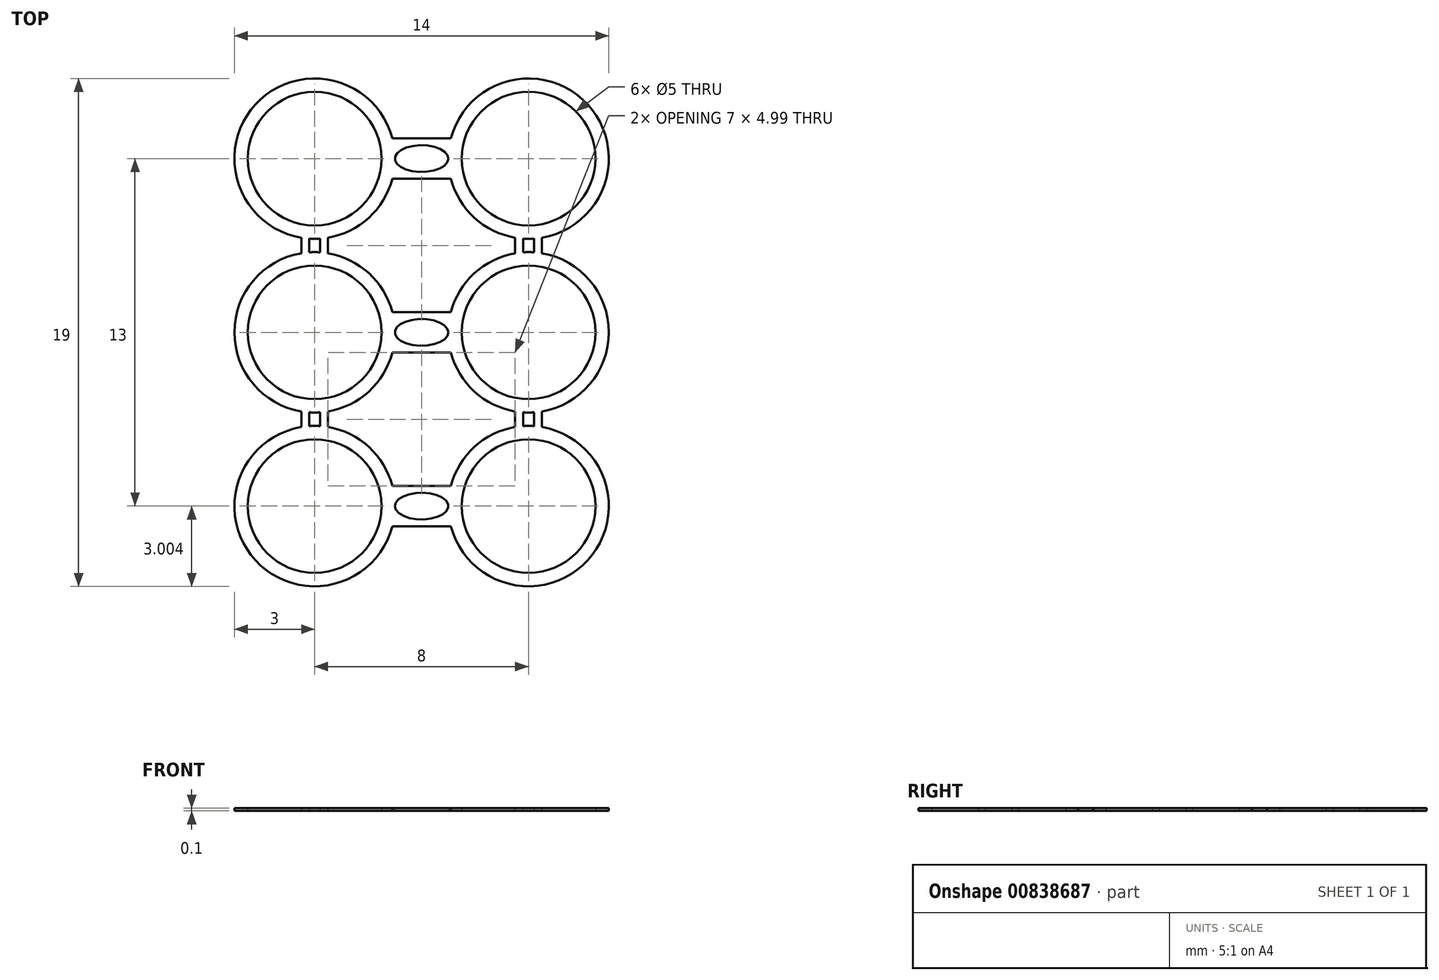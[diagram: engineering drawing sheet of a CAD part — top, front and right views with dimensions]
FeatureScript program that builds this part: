
annotation { "Feature Type Name" : "Feature", "Feature Type Description" : "" }
export const myFeature = defineFeature(function(context is Context, id is Id, definition is map)
    precondition{}
    {
        {
            var Q0;
            Q0=qCreatedBy(makeId("Top.planeOp"),FACE);
            var sketch = newSketch(context, id + "F0", { "sketchPlane" : qUnion([Q0])});
            skCircle(sketch, "E0", {"center": v(-50.37, 50.6) * mm, "radius": 3 * mm});
            skCircle(sketch, "E1", {"center": v(-50.37, 57.1) * mm, "radius": 3 * mm});
            skCircle(sketch, "E2", {"center": v(-50.37, 44.1) * mm, "radius": 3 * mm});
            skCircle(sketch, "E3", {"center": v(-42.37, 50.6) * mm, "radius": 3 * mm});
            skCircle(sketch, "E4", {"center": v(-42.37, 44.1) * mm, "radius": 3 * mm});
            skCircle(sketch, "E5", {"center": v(-42.37, 50.6) * mm, "radius": 2.5 * mm});
            skCircle(sketch, "E6", {"center": v(-50.37, 50.6) * mm, "radius": 2.5 * mm});
            skCircle(sketch, "E7", {"center": v(-50.37, 44.1) * mm, "radius": 2.5 * mm});
            skCircle(sketch, "E8", {"center": v(-42.37, 44.1) * mm, "radius": 2.5 * mm});
            skCircle(sketch, "E9", {"center": v(-50.37, 57.1) * mm, "radius": 2.5 * mm});
            skCircle(sketch, "E10", {"center": v(-42.37, 57.1) * mm, "radius": 3 * mm});
            skCircle(sketch, "E11", {"center": v(-42.37, 57.1) * mm, "radius": 2.5 * mm});
            skLineSegment(sketch, "E12", {"start": v(-47.47, 43.34) * mm, "end": v(-45.27, 43.34) * mm});
            skLineSegment(sketch, "E13", {"start": v(-47.47, 44.85) * mm, "end": v(-45.27, 44.85) * mm});
            skLineSegment(sketch, "E14", {"start": v(-47.47, 49.84) * mm, "end": v(-45.27, 49.84) * mm});
            skLineSegment(sketch, "E15", {"start": v(-47.47, 51.35) * mm, "end": v(-45.27, 51.35) * mm});
            skLineSegment(sketch, "E16", {"start": v(-47.47, 56.34) * mm, "end": v(-45.27, 56.34) * mm});
            skLineSegment(sketch, "E17", {"start": v(-47.47, 57.85) * mm, "end": v(-45.27, 57.85) * mm});
            skLineSegment(sketch, "E18", {"start": v(-42.37, 38.05) * mm, "end": v(-41.87, 38.05) * mm});
            skLineSegment(sketch, "E19", {"start": v(-49.87, 47.05) * mm, "end": v(-49.87, 47.64) * mm});
            skLineSegment(sketch, "E20", {"start": v(-50.87, 47.05) * mm, "end": v(-50.87, 47.64) * mm});
            skPoint(sketch, "E21.start.orphan", {"position": v(-50.37, 38.05) * mm});
            skLineSegment(sketch, "E22.trimOffspring", {"start": v(-42.87, 47.05) * mm, "end": v(-42.87, 47.64) * mm});
            skLineSegment(sketch, "E23.trimOffspring", {"start": v(-41.87, 47.05) * mm, "end": v(-41.87, 47.64) * mm});
            skLineSegment(sketch, "E24.trimOffspring", {"start": v(-50.87, 53.55) * mm, "end": v(-50.87, 54.14) * mm});
            skLineSegment(sketch, "E25.trimOffspring", {"start": v(-49.87, 53.55) * mm, "end": v(-49.87, 54.14) * mm});
            skLineSegment(sketch, "E26.trimOffspring", {"start": v(-42.87, 53.55) * mm, "end": v(-42.87, 54.14) * mm});
            skLineSegment(sketch, "E27.trimOffspring", {"start": v(-41.87, 53.55) * mm, "end": v(-41.87, 54.14) * mm});
            skLineSegment(sketch, "E28", {"start": v(-50.57, 47.34) * mm, "end": v(-50.57, 47.09) * mm});
            skLineSegment(sketch, "E29", {"start": v(-50.17, 47.34) * mm, "end": v(-50.17, 47.09) * mm});
            skLineSegment(sketch, "E30.trimOffspring", {"start": v(-50.57, 53.59) * mm, "end": v(-50.57, 54.1) * mm});
            skLineSegment(sketch, "E31.trimOffspring", {"start": v(-50.17, 53.59) * mm, "end": v(-50.17, 54.1) * mm});
            skLineSegment(sketch, "E32", {"start": v(-50.17, 47.34) * mm, "end": v(-50.17, 47.6) * mm});
            skLineSegment(sketch, "E33", {"start": v(-50.57, 47.34) * mm, "end": v(-50.57, 47.6) * mm});
            skLineSegment(sketch, "E34", {"start": v(-42.57, 47.09) * mm, "end": v(-42.57, 47.6) * mm});
            skLineSegment(sketch, "E35", {"start": v(-42.17, 47.09) * mm, "end": v(-42.17, 47.6) * mm});
            skLineSegment(sketch, "E36.trimOffspring", {"start": v(-42.57, 53.59) * mm, "end": v(-42.57, 54.1) * mm});
            skLineSegment(sketch, "E37.trimOffspring", {"start": v(-42.17, 53.59) * mm, "end": v(-42.17, 54.1) * mm});
            skEllipse(sketch, "E38", {"center": v(-46.37, 57.1) * mm, "majorRadius": 1 * mm, "minorRadius": 0.5 * mm, "majorAxis": v(-1, 0)});
            skPoint(sketch, "E38.centerSnap0", {"position": v(-47.47, 57.1) * mm});
            skPoint(sketch, "E38.centerSnap1", {"position": v(-46.37, 56.34) * mm});
            skEllipse(sketch, "E39.MirrorC", {"center": v(-46.37, 44.1) * mm, "majorRadius": 1 * mm, "minorRadius": 0.5 * mm, "majorAxis": v(-1, 0)});
            skEllipse(sketch, "E40.MirrorC", {"center": v(-46.37, 50.6) * mm, "majorRadius": 1 * mm, "minorRadius": 0.5 * mm, "majorAxis": v(-1, 0)});
            skSolve(sketch);
        }
        {
            var Q0;
            Q0=makeQuery(id+"F0.imprint","IMPRINT",FACE,{"disambiguationData":[TD([[makeQuery(id+"F0.imprint","IMPRINT",EDGE,{"derivedFrom":sQuery(id+"F0.wireOp",EDGE,"E7")}),-1.0]])]});
            var Q1;
            Q1=makeQuery(id+"F0.imprint","IMPRINT",FACE,{"disambiguationData":[TD([[makeQuery(id+"F0.imprint","IMPRINT",EDGE,{"derivedFrom":sQuery(id+"F0.wireOp",EDGE,"E8")}),-1.0]])]});
            var Q2;
            Q2=makeQuery(id+"F0.imprint","IMPRINT",FACE,{"disambiguationData":[TD([[makeQuery(id+"F0.imprint","IMPRINT",EDGE,{"derivedFrom":sQuery(id+"F0.wireOp",EDGE,"E5")}),-1.0]])]});
            var Q3;
            Q3=makeQuery(id+"F0.imprint","IMPRINT",FACE,{"disambiguationData":[TD([[makeQuery(id+"F0.imprint","IMPRINT",EDGE,{"derivedFrom":sQuery(id+"F0.wireOp",EDGE,"E6")}),-1.0]])]});
            var Q4;
            {var subQ0=sQuery(id+"F0.wireOp",EDGE,"E13");Q4=makeQuery(id+"F0.imprint","IMPRINT",FACE,{"disambiguationData":[TD([[makeQuery(id+"F0.imprint","IMPRINT",EDGE,{"derivedFrom":subQ0}),-1.0]])]});}
            var Q5;
            {var subQ0=sQuery(id+"F0.wireOp",EDGE,"E12");Q5=makeQuery(id+"F0.imprint","IMPRINT",FACE,{"disambiguationData":[TD([[makeQuery(id+"F0.imprint","IMPRINT",EDGE,{"derivedFrom":subQ0}),1.0]])]});}
            var Q6;
            {var subQ0=sQuery(id+"F0.wireOp",EDGE,"E15");Q6=makeQuery(id+"F0.imprint","IMPRINT",FACE,{"disambiguationData":[TD([[makeQuery(id+"F0.imprint","IMPRINT",EDGE,{"derivedFrom":subQ0}),-1.0]])]});}
            var Q7;
            {var subQ0=sQuery(id+"F0.wireOp",EDGE,"E14");Q7=makeQuery(id+"F0.imprint","IMPRINT",FACE,{"disambiguationData":[TD([[makeQuery(id+"F0.imprint","IMPRINT",EDGE,{"derivedFrom":subQ0}),1.0]])]});}
            var Q8;
            {var subQ1=sQuery(id+"F0.wireOp",EDGE,"E19");Q8=makeQuery(id+"F0.imprint","IMPRINT",FACE,{"disambiguationData":[TD([[makeQuery(id+"F0.imprint","IMPRINT",EDGE,{"derivedFrom":subQ1}),1.0]])]});}
            var Q9;
            {var subQ1=sQuery(id+"F0.wireOp",EDGE,"E20");Q9=makeQuery(id+"F0.imprint","IMPRINT",FACE,{"disambiguationData":[TD([[makeQuery(id+"F0.imprint","IMPRINT",EDGE,{"derivedFrom":subQ1}),-1.0]])]});}
            var Q10;
            {var subQ0=sQuery(id+"F0.wireOp",EDGE,"E22.trimOffspring");Q10=makeQuery(id+"F0.imprint","IMPRINT",FACE,{"disambiguationData":[TD([[makeQuery(id+"F0.imprint","IMPRINT",EDGE,{"derivedFrom":subQ0}),-1.0]])]});}
            var Q11;
            {var subQ0=sQuery(id+"F0.wireOp",EDGE,"E23.trimOffspring");Q11=makeQuery(id+"F0.imprint","IMPRINT",FACE,{"disambiguationData":[TD([[makeQuery(id+"F0.imprint","IMPRINT",EDGE,{"derivedFrom":subQ0}),1.0]])]});}
            var Q12;
            {var subQ0=sQuery(id+"F0.wireOp",EDGE,"E24.trimOffspring");Q12=makeQuery(id+"F0.imprint","IMPRINT",FACE,{"disambiguationData":[TD([[makeQuery(id+"F0.imprint","IMPRINT",EDGE,{"derivedFrom":subQ0}),-1.0]])]});}
            var Q13;
            {var subQ0=sQuery(id+"F0.wireOp",EDGE,"E25.trimOffspring");Q13=makeQuery(id+"F0.imprint","IMPRINT",FACE,{"disambiguationData":[TD([[makeQuery(id+"F0.imprint","IMPRINT",EDGE,{"derivedFrom":subQ0}),1.0]])]});}
            var Q14;
            {var subQ0=sQuery(id+"F0.wireOp",EDGE,"E26.trimOffspring");Q14=makeQuery(id+"F0.imprint","IMPRINT",FACE,{"disambiguationData":[TD([[makeQuery(id+"F0.imprint","IMPRINT",EDGE,{"derivedFrom":subQ0}),-1.0]])]});}
            var Q15;
            {var subQ0=sQuery(id+"F0.wireOp",EDGE,"E27.trimOffspring");Q15=makeQuery(id+"F0.imprint","IMPRINT",FACE,{"disambiguationData":[TD([[makeQuery(id+"F0.imprint","IMPRINT",EDGE,{"derivedFrom":subQ0}),1.0]])]});}
            var Q16;
            {var subQ0=sQuery(id+"F0.wireOp",EDGE,"E16");Q16=makeQuery(id+"F0.imprint","IMPRINT",FACE,{"disambiguationData":[TD([[makeQuery(id+"F0.imprint","IMPRINT",EDGE,{"derivedFrom":subQ0}),1.0]])]});}
            var Q17;
            {var subQ0=sQuery(id+"F0.wireOp",EDGE,"E17");Q17=makeQuery(id+"F0.imprint","IMPRINT",FACE,{"disambiguationData":[TD([[makeQuery(id+"F0.imprint","IMPRINT",EDGE,{"derivedFrom":subQ0}),-1.0]])]});}
            var Q18;
            Q18=makeQuery(id+"F0.imprint","IMPRINT",FACE,{"disambiguationData":[TD([[makeQuery(id+"F0.imprint","IMPRINT",EDGE,{"derivedFrom":sQuery(id+"F0.wireOp",EDGE,"E9")}),-1.0]])]});
            var Q19;
            Q19=makeQuery(id+"F0.imprint","IMPRINT",FACE,{"disambiguationData":[TD([[makeQuery(id+"F0.imprint","IMPRINT",EDGE,{"derivedFrom":sQuery(id+"F0.wireOp",EDGE,"E11")}),-1.0]])]});
            extrude(context, id + "F1", {"entities" : qUnion([Q0, Q1, Q2, Q3, Q4, Q5, Q6, Q7, Q8, Q9, Q10, Q11, Q12, Q13, Q14, Q15, Q16, Q17, Q18, Q19]), "endBound" : BoundingType.SYMMETRIC, "depth" : 0.1 * mm, "offsetDistance" : 25 * mm});
        }
    });
